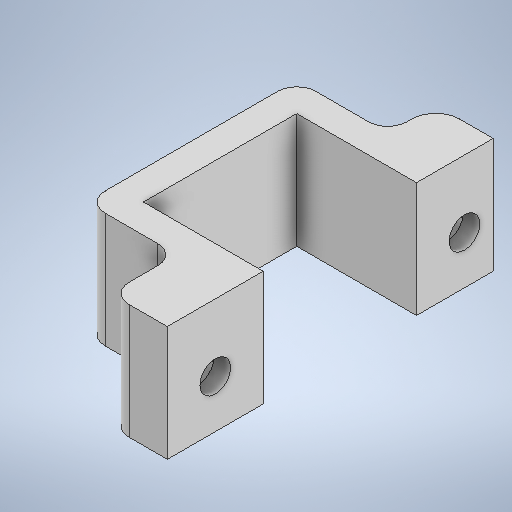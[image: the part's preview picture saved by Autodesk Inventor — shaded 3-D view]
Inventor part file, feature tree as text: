
AUTODESK INVENTOR PART (.ipt)
format: ipt  version: 2025.1 (Build 291241020, 241B)  size: 418,816 bytes
history: native  units: mm
features: extrude x7, sketch x6, plane x4, fillet x2, mirror x1, split x1, move_body x1, boolean_combine x1
ambient origin geometry x8: Origin, YZ Plane, XZ Plane, XY Plane, X Axis, Y Axis, Z Axis, Center Point
bodies: Solid1 (feature_tree), Solid2 (feature_tree), Solid3 (feature_tree)
feature tree (23):
  extrude  "Extrusion1"  Depth=16.0mm
  plane  "Work Plane1"
  sketch  "Sketch2"  dims[d3=22.0mm d4=3.0mm]
  extrude  "Extrusion2"  Depth=3.0mm
  extrude  "Extrusion3"  Depth=10.0mm
  plane  "Work Plane2"
  mirror  "Mirror1"
  extrude  "Extrusion4"  Depth=6.0mm
  plane  "Work Plane4"
  split  "Split1"
  move_body  "Move Body1"
  extrude  "Extrusion5"  [1 undecoded]
  boolean_combine  "Combine1"
  fillet  "Fillet3"  Radius=3.2mm
  extrude  "Extrusion6"  Depth=2.5mm
  extrude  "Extrusion7"  Depth=2.5mm TaperAngle=0.0deg
  fillet  "Fillet4"  Radius=0.75mm
  sketch  "Sketch1"  dims[d0=10.5mm d1=16.0mm]
  plane  "Work Plane3"
  sketch  "Sketch3"  dims[d5=10.0mm d6=10.0mm]
  sketch  "Sketch4"  dims[d7=6.0mm d8=6.0mm]
  sketch  "Sketch5"  dims[d9=14.0mm d10=0.0mm d11=-2.5mm d12=3.2mm]
  sketch  "Sketch6"  dims[d13=2.85mm d14=2.85mm d15=15.0mm d16=0.0mm d17=0.75mm d18=0.0mm d19=3.8mm d20=0.0mm d22=0.75mm d23=0.0mm d24=5.7mm d26=1.75mm d27=0.0mm d28=1.75mm d29=0.0mm d30=10.5mm d31=0.0mm d32=2.0mm d33=0.0mm d34=0.0mm d35=10.0mm d36=0.0mm d37=2.0mm d38=18.0mm d39=0.0mm d40=2.0mm d41=18.0mm d42=0.0mm d43=2.5mm d44=0.0mm d45=0.0mm d46=0.0mm]
note: 1 required parameter value undecoded (feature->parameter linkage not recoverable at this tier; creation-order binding heuristic only, values carry confidence <= 0.55)
